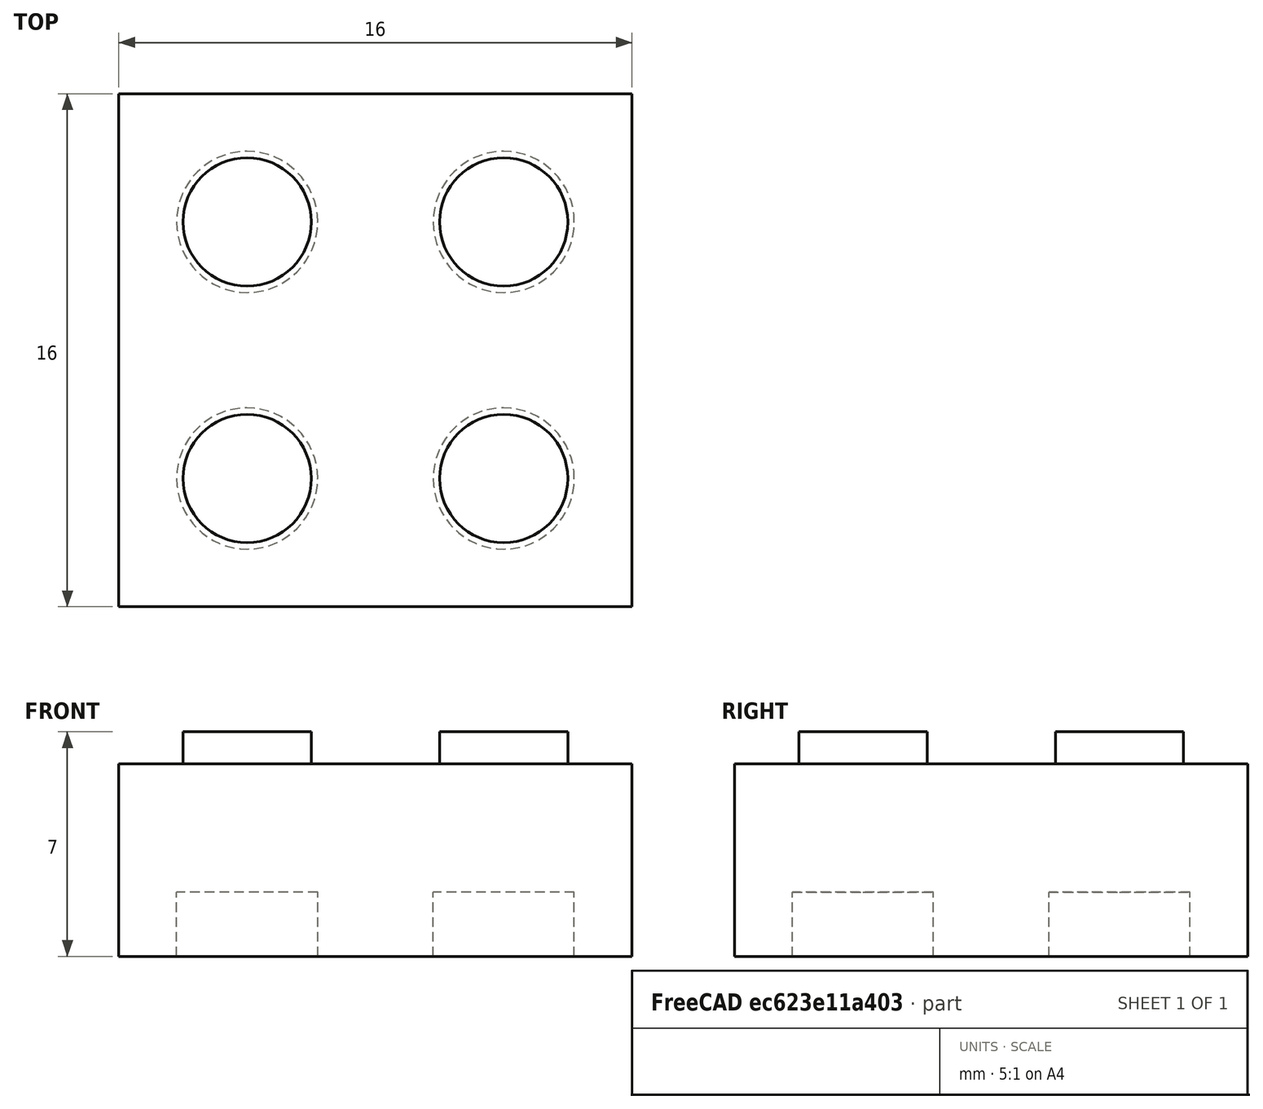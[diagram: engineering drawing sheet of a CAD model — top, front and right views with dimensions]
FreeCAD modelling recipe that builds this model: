
FCSTD DOCUMENT  (FreeCAD 0.17R13217 (Git))
Label: lego
License: All rights reserved
LicenseURL: http://en.wikipedia.org/wiki/All_rights_reserved
objects: Part::Cylinder×8, Part::MultiFuse×2, Part::Box×1, Part::Cut×1
note: 12 computed .brp shape members not serialized (recipe doc carries the construction recipe); baked Part::Feature solids carry a one-line shape summary decoded from their .brp

FEATURE [Part::Box] Box  label="Cube"
  AttacherType = Attacher::AttachEngine3D
  Height = 6
  Length = 16
  Width = 16
FEATURE [Part::Cylinder] Cylinder
  Angle = 360
  AttacherType = Attacher::AttachEngine3D
  Height = 7
  Placement = pos=(4,4,0) rot=(0,0,1;0rad)
  Radius = 2
FEATURE [Part::Cylinder] Cylinder001
  Angle = 360
  AttacherType = Attacher::AttachEngine3D
  Height = 7
  Placement = pos=(12,4,0) rot=(0,0,1;0rad)
  Radius = 2
FEATURE [Part::Cylinder] Cylinder002
  Angle = 360
  AttacherType = Attacher::AttachEngine3D
  Height = 7
  Placement = pos=(12,12,0) rot=(0,0,1;0rad)
  Radius = 2
FEATURE [Part::Cylinder] Cylinder003
  Angle = 360
  AttacherType = Attacher::AttachEngine3D
  Height = 7
  Placement = pos=(4,12,0) rot=(0,0,1;0rad)
  Radius = 2
FEATURE [Part::MultiFuse] Fusion
  Refine = true
  Shapes = -> [Box,Cylinder,Cylinder001,Cylinder002,Cylinder003]
FEATURE [Part::Cylinder] Cylinder004
  Angle = 360
  AttacherType = Attacher::AttachEngine3D
  Height = 7
  Placement = pos=(4,4,-5) rot=(0,0,1;0rad)
  Radius = 2.2
FEATURE [Part::Cylinder] Cylinder005
  Angle = 360
  AttacherType = Attacher::AttachEngine3D
  Height = 7
  Placement = pos=(4,12,-5) rot=(0,0,1;0rad)
  Radius = 2.2
FEATURE [Part::Cylinder] Cylinder006
  Angle = 360
  AttacherType = Attacher::AttachEngine3D
  Height = 7
  Placement = pos=(12,4,-5) rot=(0,0,1;0rad)
  Radius = 2.2
FEATURE [Part::Cylinder] Cylinder007
  Angle = 360
  AttacherType = Attacher::AttachEngine3D
  Height = 7
  Placement = pos=(12,12,-5) rot=(0,0,1;0rad)
  Radius = 2.2
FEATURE [Part::MultiFuse] Fusion001
  Refine = true
  Shapes = -> [Cylinder004,Cylinder007,Cylinder005,Cylinder006]
FEATURE [Part::Cut] Cut
  Base = -> Fusion
  Refine = true
  Tool = -> Fusion001
